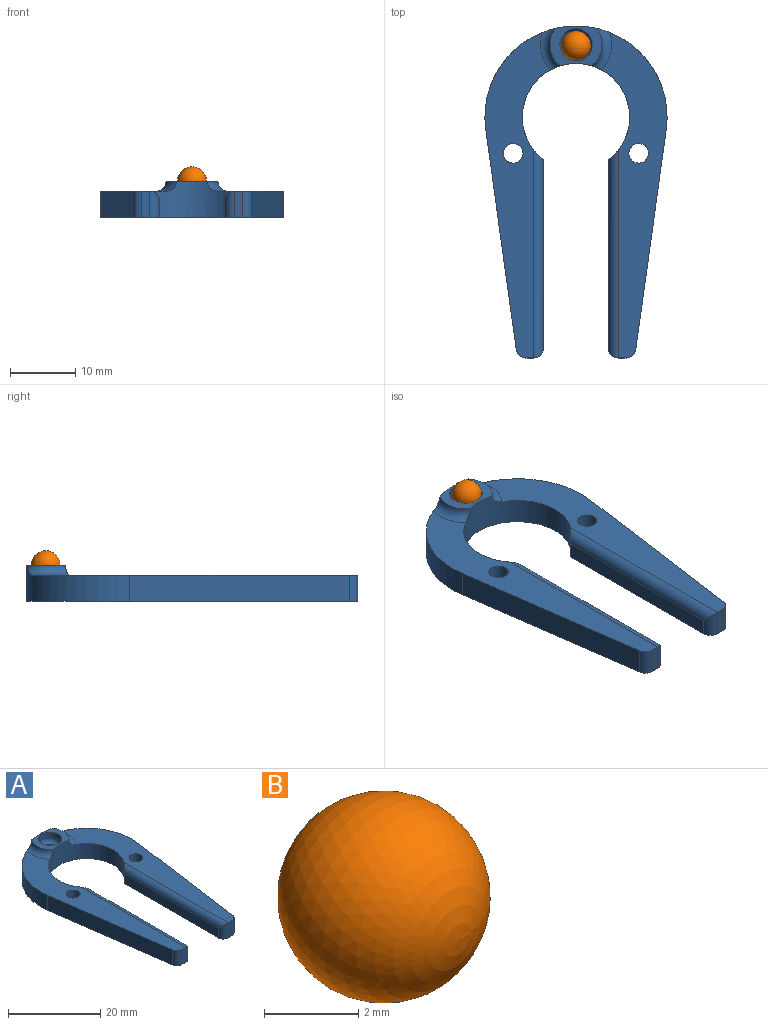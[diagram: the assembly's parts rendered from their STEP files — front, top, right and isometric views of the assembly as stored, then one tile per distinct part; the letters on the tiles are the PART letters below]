
ASSEMBLY  parts=2 mates=1
PART A: 25 faces, bbox 28x52.6x6.6 mm
  f0: cylinder r=1.5mm len=3mm, axis (0,0,-1), area 28.3mm2, adj f13,f16
  f1: plane 50.01x10.09mm, normal (0,0,1), area 244.1mm2, adj f3,f5,f6,f7,f10,f18,f22,f24
  f2: plane 28.94x2.5mm, normal (1,0,0), area 72.3mm2, adj f3,f13,f20,f21
  f3: cylinder r=8.25mm len=16.5mm, axis (0,0,-1), area 171.4mm2, adj f1,f2,f4,f12,f13,f14,f17,f18
  f4: plane 28.94x2.5mm, normal (-1,0,0), area 72.3mm2, adj f3,f13,f22,f23
  f5: plane 4x1.19mm, normal (0,-1,0), area 4.8mm2, adj f1,f13,f23,f24
  f6: plane 33.78x4.69mm, normal (0.99,-0.14,0), area 136.4mm2, adj f1,f7,f13,f24
  f7: cylinder r=14mm len=28mm, axis (0,0,-1), area 202.2mm2, adj f1,f6,f8,f12,f13,f14,f17,f18
  f8: plane 33.78x4.69mm, normal (-0.99,-0.14,0), area 136.4mm2, adj f7,f12,f13,f19
  f9: cylinder r=1.5mm len=4mm, axis (0,0,-1), area 37.7mm2, adj f12,f13
  f10: cylinder r=1.5mm len=4mm, axis (0,0,-1), area 37.7mm2, adj f1,f13
  f11: plane 4x1.19mm, normal (0,-1,0), area 4.8mm2, adj f12,f13,f19,f21
  f12: plane 50.01x10.09mm, normal (0,0,1), area 244.1mm2, adj f3,f7,f8,f9,f11,f17,f19,f20
  f13: plane 51x28mm, normal (0,0,-1), area 634.1mm2, adj f0,f2,f3,f4,f5,f6,f7,f8
  f14: plane 8x6.1mm, normal (0,0,1), area 22.1mm2, adj f3,f7,f15,f17,f18
  f15: cylinder r=2.5mm len=5mm, axis (0,0,1), area 23.6mm2, adj f14,f16
  f16: torus R=1.5mm, axis (0,0,1), area 21.1mm2, adj f0,f15
  f17: torus R=5.5mm, axis (0,0,1), area 14.9mm2, adj f3,f7,f12,f14
  f18: torus R=5.5mm, axis (0,0,1), area 14.9mm2, adj f1,f3,f7,f14
  f19: cylinder r=1.5mm len=4mm, axis (0,0,-1), area 8.6mm2, adj f8,f11,f12,f13
  f20: cylinder r=1.5mm len=31.92mm, axis (0,-1,0), area 71.6mm2, adj f2,f3,f12,f21
  f21: cylinder r=1.5mm len=4mm, axis (0,0,-1), area 8.1mm2, adj f2,f11,f13,f20
  f22: cylinder r=1.5mm len=31.92mm, axis (0,1,0), area 71.6mm2, adj f1,f3,f4,f23
  f23: cylinder r=1.5mm len=4mm, axis (0,0,-1), area 8.1mm2, adj f4,f5,f13,f22
  f24: cylinder r=1.5mm len=4mm, axis (0,0,-1), area 8.6mm2, adj f1,f5,f6,f13
PART B: 1 faces, bbox 4.5x4.5x4.5 mm
  f0: sphere r=2.25mm, area 63.6mm2
PLACE A t=(-4.22,-8.58,-0.76)mm
PLACE B t=(-4.22,2.37,4.74)mm
MATE ball A.f14 <-> B.f0  axis (0,0,1) through (-4.22,2.37,4.74)mm
